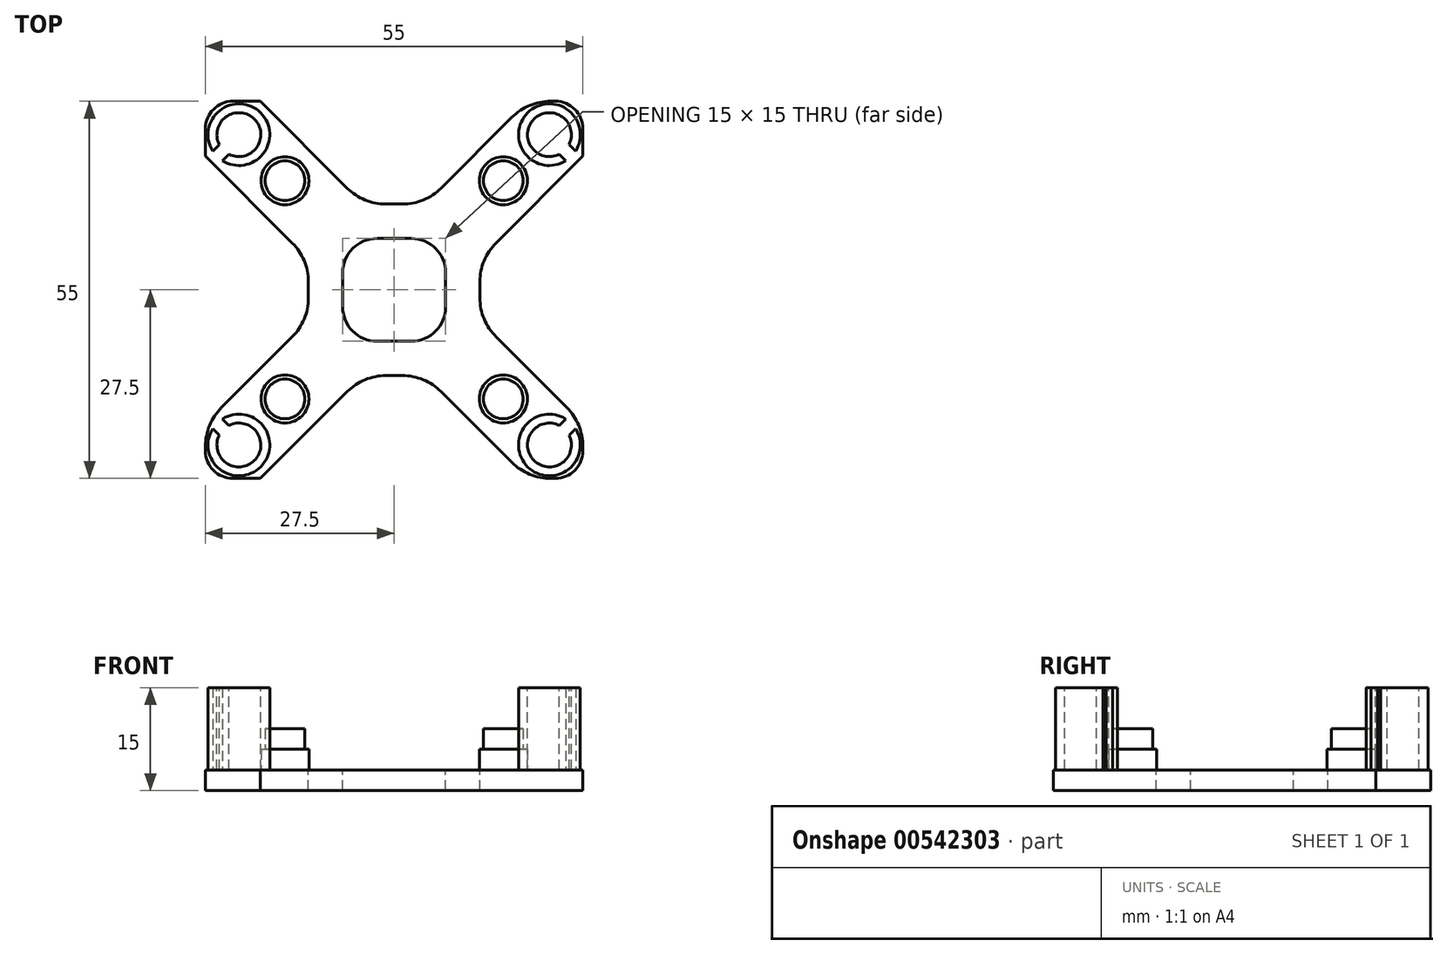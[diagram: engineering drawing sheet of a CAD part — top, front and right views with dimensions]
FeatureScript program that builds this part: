
annotation { "Feature Type Name" : "Feature", "Feature Type Description" : "" }
export const myFeature = defineFeature(function(context is Context, id is Id, definition is map)
    precondition{}
    {
        {
            var Q0;
            Q0=qCreatedBy(makeId("Top.planeOp"),FACE);
            var sketch = newSketch(context, id + "F0", { "sketchPlane" : qUnion([Q0])});
            skLineSegment(sketch, "E0.bottom", {"start": v(-27.5, 27.5) * mm, "end": v(27.5, 27.5) * mm});
            skLineSegment(sketch, "E0.top", {"start": v(-27.5, -27.5) * mm, "end": v(27.5, -27.5) * mm});
            skLineSegment(sketch, "E0.left", {"start": v(-27.5, 27.5) * mm, "end": v(-27.5, -27.5) * mm});
            skLineSegment(sketch, "E0.right", {"start": v(27.5, 27.5) * mm, "end": v(27.5, -27.5) * mm});
            skPoint(sketch, "E0.middle", {"position": v(0, 0) * mm});
            skLineSegment(sketch, "E1", {"start": v(-27.5, 27.5) * mm, "end": v(27.5, -27.5) * mm, "construction": true});
            skLineSegment(sketch, "E2", {"start": v(27.5, 27.5) * mm, "end": v(-27.5, -27.5) * mm, "construction": true});
            skSolve(sketch);
        }
        {
            var Q0;
            Q0=qSketchRegion(id+"F0",true);
            extrude(context, id + "F1", {"entities" : qUnion([Q0]), "depth" : 3 * mm, "offsetDistance" : 25 * mm});
        }
        {
            var Q0;
            Q0=makeQuery(id+"F1.opExtrude","CAP_FACE",FACE,{"disambiguationData":[OSD([sQuery(id+"F0.wireOp",EDGE,"E0.bottom"),sQuery(id+"F0.wireOp",EDGE,"E0.top"),sQuery(id+"F0.wireOp",EDGE,"E0.left"),sQuery(id+"F0.wireOp",EDGE,"E0.right")])],"isStart":false});
            var sketch = newSketch(context, id + "F2", { "sketchPlane" : qUnion([Q0])});
            skLineSegment(sketch, "E3", {"start": v(-27.5, 27.5) * mm, "end": v(27.5, -27.5) * mm, "construction": true});
            skLineSegment(sketch, "E4", {"start": v(27.5, 27.5) * mm, "end": v(-27.5, -27.5) * mm, "construction": true});
            skCircle(sketch, "E5", {"center": v(-15.9, 15.9) * mm, "radius": 3.5 * mm});
            skCircle(sketch, "E6", {"center": v(15.9, 15.9) * mm, "radius": 3.5 * mm});
            skCircle(sketch, "E7", {"center": v(-15.9, -15.9) * mm, "radius": 3.5 * mm});
            skCircle(sketch, "E8", {"center": v(15.9, -15.9) * mm, "radius": 3.5 * mm});
            skSolve(sketch);
        }
        {
            var Q0;
            Q0=qSketchRegion(id+"F2",true);
            extrude(context, id + "F3", {"entities" : qUnion([Q0]), "operationType" : NewBodyOperationType.ADD, "depth" : 3 * mm, "offsetDistance" : 25 * mm});
        }
        {
            var Q0;
            Q0=makeQuery(id+"F3.opExtrude","CAP_FACE",FACE,{"disambiguationData":[OSD([sQuery(id+"F2.wireOp",EDGE,"E5")])],"isStart":false});
            var sketch = newSketch(context, id + "F4", { "sketchPlane" : qUnion([Q0])});
            skCircle(sketch, "E9", {"center": v(-15.9, 15.9) * mm, "radius": 2.9 * mm});
            skCircle(sketch, "E10", {"center": v(15.9, 15.9) * mm, "radius": 2.9 * mm});
            skCircle(sketch, "E11", {"center": v(-15.9, -15.9) * mm, "radius": 2.9 * mm});
            skCircle(sketch, "E12", {"center": v(15.9, -15.9) * mm, "radius": 2.9 * mm});
            skSolve(sketch);
        }
        {
            var Q0;
            Q0=qSketchRegion(id+"F4",true);
            extrude(context, id + "F5", {"entities" : qUnion([Q0]), "operationType" : NewBodyOperationType.ADD, "depth" : 3 * mm, "offsetDistance" : 25 * mm});
        }
        {
            var Q0;
            Q0=makeQuery(id+"F1.opExtrude","CAP_FACE",FACE,{"disambiguationData":[OSD([sQuery(id+"F0.wireOp",EDGE,"E0.bottom"),sQuery(id+"F0.wireOp",EDGE,"E0.top"),sQuery(id+"F0.wireOp",EDGE,"E0.left"),sQuery(id+"F0.wireOp",EDGE,"E0.right")])],"isStart":false});
            var sketch = newSketch(context, id + "F6", { "sketchPlane" : qUnion([Q0])});
            skLineSegment(sketch, "E13", {"start": v(-27.5, 27.5) * mm, "end": v(27.5, -27.5) * mm, "construction": true});
            skLineSegment(sketch, "E14", {"start": v(27.5, 27.5) * mm, "end": v(-27.5, -27.5) * mm, "construction": true});
            skCircle(sketch, "E15", {"center": v(-22.63, 22.63) * mm, "radius": 4.5 * mm});
            skCircle(sketch, "E16", {"center": v(22.63, 22.63) * mm, "radius": 4.5 * mm});
            skCircle(sketch, "E17", {"center": v(22.63, -22.63) * mm, "radius": 4.5 * mm});
            skCircle(sketch, "E18", {"center": v(-22.63, -22.63) * mm, "radius": 4.5 * mm});
            skSolve(sketch);
        }
        {
            var Q0;
            Q0=qSketchRegion(id+"F6",true);
            extrude(context, id + "F7", {"entities" : qUnion([Q0]), "operationType" : NewBodyOperationType.ADD, "depth" : 12 * mm, "offsetDistance" : 25 * mm});
        }
        {
            var Q0;
            Q0=makeQuery(id+"F7.opExtrude","CAP_FACE",FACE,{"disambiguationData":[OSD([sQuery(id+"F6.wireOp",EDGE,"E18")])],"isStart":false});
            var sketch = newSketch(context, id + "F8", { "sketchPlane" : qUnion([Q0])});
            skCircle(sketch, "E19", {"center": v(-22.63, -22.63) * mm, "radius": 3.2 * mm});
            skCircle(sketch, "E20", {"center": v(22.63, -22.63) * mm, "radius": 3.2 * mm});
            skCircle(sketch, "E21", {"center": v(-22.63, 22.63) * mm, "radius": 3.2 * mm});
            skCircle(sketch, "E22", {"center": v(22.63, 22.63) * mm, "radius": 3.2 * mm});
            skSolve(sketch);
        }
        {
            var Q0;
            Q0=qSketchRegion(id+"F8",true);
            extrude(context, id + "F9", {"entities" : qUnion([Q0]), "operationType" : NewBodyOperationType.REMOVE, "oppositeDirection" : true, "depth" : 12 * mm, "offsetDistance" : 25 * mm});
        }
        {
            var Q0;
            Q0=makeQuery(id+"F1.opExtrude","SWEPT_EDGE",EDGE,{"disambiguationData":[OSD([sQuery(id+"F0.wireOp",EDGE,"E0.top"),sQuery(id+"F0.wireOp",EDGE,"E0.right")])]});
            var Q1;
            Q1=makeQuery(id+"F1.opExtrude","SWEPT_EDGE",EDGE,{"disambiguationData":[OSD([sQuery(id+"F0.wireOp",EDGE,"E0.top"),sQuery(id+"F0.wireOp",EDGE,"E0.left")])]});
            var Q2;
            Q2=makeQuery(id+"F1.opExtrude","SWEPT_EDGE",EDGE,{"disambiguationData":[OSD([sQuery(id+"F0.wireOp",EDGE,"E0.bottom"),sQuery(id+"F0.wireOp",EDGE,"E0.left")])]});
            var Q3;
            Q3=makeQuery(id+"F1.opExtrude","SWEPT_EDGE",EDGE,{"disambiguationData":[OSD([sQuery(id+"F0.wireOp",EDGE,"E0.bottom"),sQuery(id+"F0.wireOp",EDGE,"E0.right")])]});
            fillet(context, id + "F10", {"entities" : qUnion([Q0, Q1, Q2, Q3]), "radius" : 4 * mm, "tangentPropagation" : true, "allowEdgeOverflow" : false});
        }
        {
            var Q0;
            Q0=makeQuery(id+"F1.opExtrude","CAP_FACE",FACE,{"disambiguationData":[OSD([sQuery(id+"F0.wireOp",EDGE,"E0.bottom"),sQuery(id+"F0.wireOp",EDGE,"E0.top"),sQuery(id+"F0.wireOp",EDGE,"E0.left"),sQuery(id+"F0.wireOp",EDGE,"E0.right")])],"isStart":false});
            var sketch = newSketch(context, id + "F11", { "sketchPlane" : qUnion([Q0])});
            skLineSegment(sketch, "E23.0", {"start": v(-27.5, 27.5) * mm, "end": v(27.5, -27.5) * mm, "construction": true});
            skLineSegment(sketch, "E24.0", {"start": v(27.5, 27.5) * mm, "end": v(-27.5, -27.5) * mm, "construction": true});
            skPoint(sketch, "E25.middle", {"position": v(0, 0) * mm});
            skLineSegment(sketch, "E26", {"start": v(-12.5, 12.5) * mm, "end": v(12.5, 12.5) * mm, "construction": true});
            skLineSegment(sketch, "E27", {"start": v(-12.5, 12.5) * mm, "end": v(-12.5, -12.5) * mm, "construction": true});
            skLineSegment(sketch, "E28", {"start": v(-12.5, -12.5) * mm, "end": v(12.5, -12.5) * mm, "construction": true});
            skLineSegment(sketch, "E29", {"start": v(12.5, -12.5) * mm, "end": v(12.5, 12.5) * mm, "construction": true});
            skLineSegment(sketch, "E30", {"start": v(-27.5, 19.5) * mm, "end": v(-12.5, 4.5) * mm});
            skLineSegment(sketch, "E31", {"start": v(-12.5, 4.5) * mm, "end": v(-12.5, -4.5) * mm});
            skLineSegment(sketch, "E32", {"start": v(-12.5, -4.5) * mm, "end": v(-27.5, -19.5) * mm});
            skLineSegment(sketch, "E33", {"start": v(-27.5, -19.5) * mm, "end": v(-27.5, 19.5) * mm});
            skLineSegment(sketch, "E34", {"start": v(-19.5, 27.5) * mm, "end": v(-4.5, 12.5) * mm});
            skLineSegment(sketch, "E35", {"start": v(-4.5, 12.5) * mm, "end": v(4.5, 12.5) * mm});
            skLineSegment(sketch, "E36", {"start": v(4.5, 12.5) * mm, "end": v(19.5, 27.5) * mm});
            skLineSegment(sketch, "E37", {"start": v(19.5, 27.5) * mm, "end": v(-19.5, 27.5) * mm});
            skLineSegment(sketch, "E38", {"start": v(27.5, 19.5) * mm, "end": v(12.5, 4.5) * mm});
            skLineSegment(sketch, "E39", {"start": v(12.5, 4.5) * mm, "end": v(12.5, -4.5) * mm});
            skLineSegment(sketch, "E40", {"start": v(12.5, -4.5) * mm, "end": v(27.5, -19.5) * mm});
            skLineSegment(sketch, "E41", {"start": v(27.5, -19.5) * mm, "end": v(27.5, 19.5) * mm});
            skLineSegment(sketch, "E42", {"start": v(-19.5, -27.5) * mm, "end": v(-4.5, -12.5) * mm});
            skLineSegment(sketch, "E43", {"start": v(-4.5, -12.5) * mm, "end": v(4.5, -12.5) * mm});
            skLineSegment(sketch, "E44", {"start": v(4.5, -12.5) * mm, "end": v(19.5, -27.5) * mm});
            skLineSegment(sketch, "E45", {"start": v(19.5, -27.5) * mm, "end": v(-19.5, -27.5) * mm});
            skLineSegment(sketch, "E46.bottom", {"start": v(7.5, -7.5) * mm, "end": v(-7.5, -7.5) * mm});
            skLineSegment(sketch, "E46.top", {"start": v(7.5, 7.5) * mm, "end": v(-7.5, 7.5) * mm});
            skLineSegment(sketch, "E46.left", {"start": v(7.5, -7.5) * mm, "end": v(7.5, 7.5) * mm});
            skLineSegment(sketch, "E46.right", {"start": v(-7.5, -7.5) * mm, "end": v(-7.5, 7.5) * mm});
            skSolve(sketch);
        }
        {
            var Q0;
            Q0 = qSketchRegion(id + "F11", true);
            extrude(context, id + "F12", {"entities" : qUnion([Q0]), "operationType" : NewBodyOperationType.REMOVE, "endBound" : BoundingType.SYMMETRIC, "oppositeDirection" : true, "depth" : 40 * mm, "offsetDistance" : 25 * mm});
        }
        {
            var Q0;
            Q0=makeQuery(id+"F1.opExtrude","CAP_FACE",FACE,{"disambiguationData":[OSD([sQuery(id+"F0.wireOp",EDGE,"E0.bottom"),sQuery(id+"F0.wireOp",EDGE,"E0.top"),sQuery(id+"F0.wireOp",EDGE,"E0.left"),sQuery(id+"F0.wireOp",EDGE,"E0.right")])],"isStart":false});
            var sketch = newSketch(context, id + "F13", { "sketchPlane" : qUnion([Q0])});
            skLineSegment(sketch, "E47", {"start": v(-14.9, 30.35) * mm, "end": v(-30.28, 14.98) * mm, "construction": true});
            skLineSegment(sketch, "E48", {"start": v(-22.63, 22.63) * mm, "end": v(22.63, 22.63) * mm, "construction": true});
            skPoint(sketch, "E49.cornerSnap0", {"position": v(-27.5, 21.5) * mm});
            skLineSegment(sketch, "E50", {"start": v(-25.43, 18.4) * mm, "end": v(-22.6, 21.24) * mm});
            skLineSegment(sketch, "E51", {"start": v(-22.6, 21.24) * mm, "end": v(-24.02, 22.65) * mm});
            skLineSegment(sketch, "E52", {"start": v(-24.02, 22.65) * mm, "end": v(-26.85, 19.82) * mm});
            skLineSegment(sketch, "E53", {"start": v(-26.85, 19.82) * mm, "end": v(-25.43, 18.4) * mm});
            skLineSegment(sketch, "E54.MirrorCS", {"start": v(25.43, 18.4) * mm, "end": v(22.6, 21.24) * mm});
            skLineSegment(sketch, "E55.MirrorCS", {"start": v(26.85, 19.82) * mm, "end": v(25.43, 18.4) * mm});
            skLineSegment(sketch, "E56.MirrorCS", {"start": v(22.6, 21.24) * mm, "end": v(24.02, 22.65) * mm});
            skLineSegment(sketch, "E57.MirrorCS", {"start": v(24.02, 22.65) * mm, "end": v(26.85, 19.82) * mm});
            skLineSegment(sketch, "E58.MirrorCS", {"start": v(-26.85, -19.82) * mm, "end": v(-25.43, -18.4) * mm});
            skLineSegment(sketch, "E59.MirrorCS", {"start": v(-24.02, -22.65) * mm, "end": v(-26.85, -19.82) * mm});
            skLineSegment(sketch, "E60.MirrorCS", {"start": v(-22.6, -21.24) * mm, "end": v(-24.02, -22.65) * mm});
            skLineSegment(sketch, "E61.MirrorCS", {"start": v(-25.43, -18.4) * mm, "end": v(-22.6, -21.24) * mm});
            skLineSegment(sketch, "E62.MirrorCS", {"start": v(25.43, -18.4) * mm, "end": v(22.6, -21.24) * mm});
            skLineSegment(sketch, "E63.MirrorCS", {"start": v(24.02, -22.65) * mm, "end": v(26.85, -19.82) * mm});
            skLineSegment(sketch, "E64.MirrorCS", {"start": v(26.85, -19.82) * mm, "end": v(25.43, -18.4) * mm});
            skLineSegment(sketch, "E65.MirrorCS", {"start": v(22.6, -21.24) * mm, "end": v(24.02, -22.65) * mm});
            skSolve(sketch);
        }
        {
            var Q0;
            Q0 = qSketchRegion(id + "F13", true);
            extrude(context, id + "F14", {"entities" : qUnion([Q0]), "operationType" : NewBodyOperationType.REMOVE, "depth" : 25 * mm, "offsetDistance" : 25 * mm});
        }
        {
            var Q0;
            Q0=makeQuery(id+"F12.boolean.opBoolean","COPY",EDGE,{"derivedFrom":makeQuery(id+"F12.opExtrude","SWEPT_EDGE",EDGE,{"disambiguationData":[OSD([sQuery(id+"F0.wireOp",EDGE,"E0.top"),sQuery(id+"F11.wireOp",EDGE,"E44"),sQuery(id+"F11.wireOp",EDGE,"E45")])]})});
            var Q1;
            Q1=makeQuery(id+"F12.boolean.opBoolean","COPY",EDGE,{"derivedFrom":makeQuery(id+"F12.opExtrude","SWEPT_EDGE",EDGE,{"disambiguationData":[OSD([sQuery(id+"F11.wireOp",EDGE,"E43"),sQuery(id+"F11.wireOp",EDGE,"E44")])]})});
            var Q2;
            Q2=makeQuery(id+"F12.boolean.opBoolean","COPY",EDGE,{"derivedFrom":makeQuery(id+"F12.opExtrude","SWEPT_EDGE",EDGE,{"disambiguationData":[OSD([sQuery(id+"F11.wireOp",EDGE,"E42"),sQuery(id+"F11.wireOp",EDGE,"E43")])]})});
            var Q3;
            Q3=makeQuery(id+"F12.boolean.opBoolean","COPY",EDGE,{"derivedFrom":makeQuery(id+"F12.opExtrude","SWEPT_EDGE",EDGE,{"disambiguationData":[OSD([sQuery(id+"F0.wireOp",EDGE,"E0.top"),sQuery(id+"F11.wireOp",EDGE,"E42"),sQuery(id+"F11.wireOp",EDGE,"E45")])]})});
            var Q4;
            Q4=makeQuery(id+"F12.boolean.opBoolean","COPY",EDGE,{"derivedFrom":makeQuery(id+"F12.opExtrude","SWEPT_EDGE",EDGE,{"disambiguationData":[OSD([sQuery(id+"F0.wireOp",EDGE,"E0.left"),sQuery(id+"F11.wireOp",EDGE,"E32"),sQuery(id+"F11.wireOp",EDGE,"E33")])]})});
            var Q5;
            Q5=makeQuery(id+"F12.boolean.opBoolean","COPY",EDGE,{"derivedFrom":makeQuery(id+"F12.opExtrude","SWEPT_EDGE",EDGE,{"disambiguationData":[OSD([sQuery(id+"F11.wireOp",EDGE,"E31"),sQuery(id+"F11.wireOp",EDGE,"E32")])]})});
            var Q6;
            Q6=makeQuery(id+"F12.boolean.opBoolean","COPY",EDGE,{"derivedFrom":makeQuery(id+"F12.opExtrude","SWEPT_EDGE",EDGE,{"disambiguationData":[OSD([sQuery(id+"F11.wireOp",EDGE,"E30"),sQuery(id+"F11.wireOp",EDGE,"E31")])]})});
            var Q7;
            Q7=makeQuery(id+"F12.boolean.opBoolean","COPY",EDGE,{"derivedFrom":makeQuery(id+"F12.opExtrude","SWEPT_EDGE",EDGE,{"disambiguationData":[OSD([sQuery(id+"F0.wireOp",EDGE,"E0.left"),sQuery(id+"F11.wireOp",EDGE,"E30"),sQuery(id+"F11.wireOp",EDGE,"E33")])]})});
            var Q8;
            Q8=makeQuery(id+"F12.boolean.opBoolean","COPY",EDGE,{"derivedFrom":makeQuery(id+"F12.opExtrude","SWEPT_EDGE",EDGE,{"disambiguationData":[OSD([sQuery(id+"F0.wireOp",EDGE,"E0.bottom"),sQuery(id+"F11.wireOp",EDGE,"E34"),sQuery(id+"F11.wireOp",EDGE,"E37")])]})});
            var Q9;
            Q9=makeQuery(id+"F12.boolean.opBoolean","COPY",EDGE,{"derivedFrom":makeQuery(id+"F12.opExtrude","SWEPT_EDGE",EDGE,{"disambiguationData":[OSD([sQuery(id+"F11.wireOp",EDGE,"E34"),sQuery(id+"F11.wireOp",EDGE,"E35")])]})});
            var Q10;
            Q10=makeQuery(id+"F12.boolean.opBoolean","COPY",EDGE,{"derivedFrom":makeQuery(id+"F12.opExtrude","SWEPT_EDGE",EDGE,{"disambiguationData":[OSD([sQuery(id+"F11.wireOp",EDGE,"E35"),sQuery(id+"F11.wireOp",EDGE,"E36")])]})});
            var Q11;
            Q11=makeQuery(id+"F12.boolean.opBoolean","COPY",EDGE,{"derivedFrom":makeQuery(id+"F12.opExtrude","SWEPT_EDGE",EDGE,{"disambiguationData":[OSD([sQuery(id+"F0.wireOp",EDGE,"E0.bottom"),sQuery(id+"F11.wireOp",EDGE,"E36"),sQuery(id+"F11.wireOp",EDGE,"E37")])]})});
            var Q12;
            Q12=makeQuery(id+"F12.boolean.opBoolean","COPY",EDGE,{"derivedFrom":makeQuery(id+"F12.opExtrude","SWEPT_EDGE",EDGE,{"disambiguationData":[OSD([sQuery(id+"F11.wireOp",EDGE,"E39"),sQuery(id+"F11.wireOp",EDGE,"E40")])]})});
            var Q13;
            Q13=makeQuery(id+"F12.boolean.opBoolean","COPY",EDGE,{"derivedFrom":makeQuery(id+"F12.opExtrude","SWEPT_EDGE",EDGE,{"disambiguationData":[OSD([sQuery(id+"F11.wireOp",EDGE,"E38"),sQuery(id+"F11.wireOp",EDGE,"E39")])]})});
            var Q14;
            Q14=makeQuery(id+"F12.boolean.opBoolean","COPY",EDGE,{"derivedFrom":makeQuery(id+"F12.opExtrude","SWEPT_EDGE",EDGE,{"disambiguationData":[OSD([sQuery(id+"F0.wireOp",EDGE,"E0.right"),sQuery(id+"F11.wireOp",EDGE,"E38"),sQuery(id+"F11.wireOp",EDGE,"E41")])]})});
            var Q15;
            Q15=makeQuery(id+"F12.boolean.opBoolean","COPY",EDGE,{"derivedFrom":makeQuery(id+"F12.opExtrude","SWEPT_EDGE",EDGE,{"disambiguationData":[OSD([sQuery(id+"F0.wireOp",EDGE,"E0.right"),sQuery(id+"F11.wireOp",EDGE,"E40"),sQuery(id+"F11.wireOp",EDGE,"E41")])]})});
            fillet(context, id + "F15", {"entities" : qUnion([Q0, Q1, Q2, Q3, Q4, Q5, Q6, Q7, Q8, Q9, Q10, Q11, Q12, Q13, Q14, Q15]), "radius" : 8 * mm, "tangentPropagation" : true, "allowEdgeOverflow" : false});
        }
        {
            var Q0;
            Q0=makeQuery(id+"F12.boolean.opBoolean","COPY",EDGE,{"derivedFrom":makeQuery(id+"F12.opExtrude","SWEPT_EDGE",EDGE,{"disambiguationData":[OSD([sQuery(id+"F11.wireOp",EDGE,"E46.top"),sQuery(id+"F11.wireOp",EDGE,"E46.right")])]})});
            var Q1;
            Q1=makeQuery(id+"F12.boolean.opBoolean","COPY",EDGE,{"derivedFrom":makeQuery(id+"F12.opExtrude","SWEPT_EDGE",EDGE,{"disambiguationData":[OSD([sQuery(id+"F11.wireOp",EDGE,"E46.top"),sQuery(id+"F11.wireOp",EDGE,"E46.left")])]})});
            var Q2;
            Q2=makeQuery(id+"F12.boolean.opBoolean","COPY",EDGE,{"derivedFrom":makeQuery(id+"F12.opExtrude","SWEPT_EDGE",EDGE,{"disambiguationData":[OSD([sQuery(id+"F11.wireOp",EDGE,"E46.bottom"),sQuery(id+"F11.wireOp",EDGE,"E46.left")])]})});
            var Q3;
            Q3=makeQuery(id+"F12.boolean.opBoolean","COPY",EDGE,{"derivedFrom":makeQuery(id+"F12.opExtrude","SWEPT_EDGE",EDGE,{"disambiguationData":[OSD([sQuery(id+"F11.wireOp",EDGE,"E46.bottom"),sQuery(id+"F11.wireOp",EDGE,"E46.right")])]})});
            fillet(context, id + "F16", {"entities" : qUnion([Q0, Q1, Q2, Q3]), "radius" : 5 * mm, "tangentPropagation" : true, "allowEdgeOverflow" : false});
        }
    });
